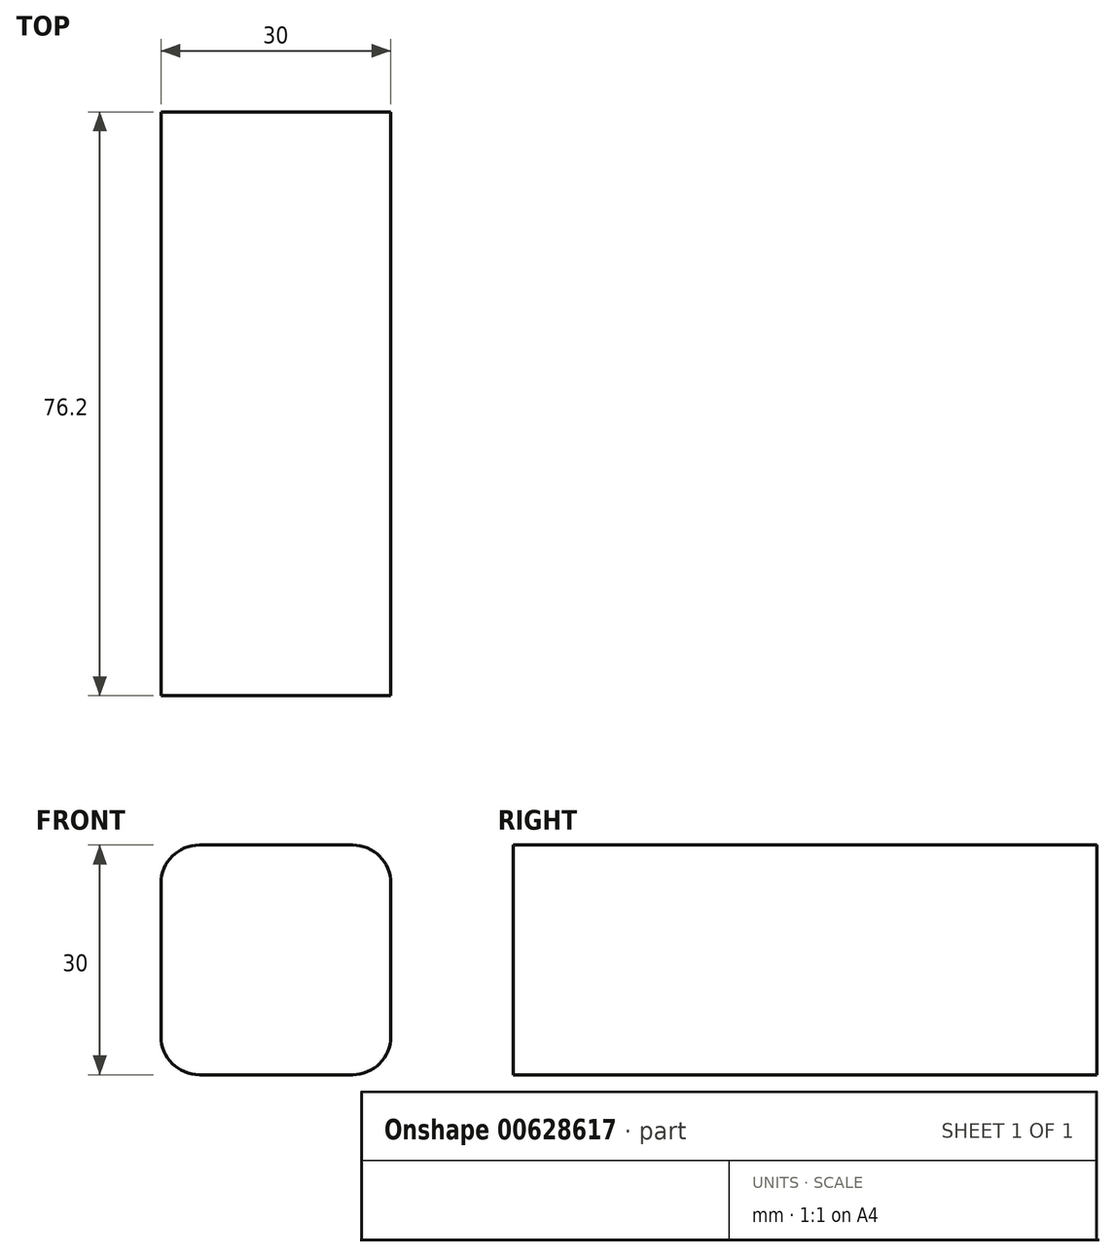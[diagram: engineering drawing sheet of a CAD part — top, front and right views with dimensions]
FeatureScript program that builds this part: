
annotation { "Feature Type Name" : "Feature", "Feature Type Description" : "" }
export const myFeature = defineFeature(function(context is Context, id is Id, definition is map)
    precondition{}
    {
        {
            var Q0;
            Q0=qCreatedBy(makeId("Front.planeOp"),FACE);
            var sketch = newSketch(context, id + "F0", { "sketchPlane" : qUnion([Q0])});
            skLineSegment(sketch, "E0.bottom", {"start": v(-92.2, 23.85) * mm, "end": v(-62.2, 23.85) * mm});
            skLineSegment(sketch, "E0.top", {"start": v(-92.2, -6.15) * mm, "end": v(-62.2, -6.15) * mm});
            skLineSegment(sketch, "E0.left", {"start": v(-92.2, 23.85) * mm, "end": v(-92.2, -6.15) * mm});
            skLineSegment(sketch, "E0.right", {"start": v(-62.2, 23.85) * mm, "end": v(-62.2, -6.15) * mm});
            skSolve(sketch);
        }
        {
            var Q0;
            Q0 = qSketchRegion(id + "F0", true);
            extrude(context, id + "F1", {"entities" : qUnion([Q0]), "depth" : 76.2 * mm, "offsetDistance" : 25.4 * mm});
        }
        {
            var Q0;
            Q0=makeQuery(id+"F1.opExtrude","SWEPT_EDGE",EDGE,{"disambiguationData":[OSD([sQuery(id+"F0.wireOp",EDGE,"E0.bottom"),sQuery(id+"F0.wireOp",EDGE,"E0.right")])]});
            var Q1;
            Q1=makeQuery(id+"F1.opExtrude","SWEPT_EDGE",EDGE,{"disambiguationData":[OSD([sQuery(id+"F0.wireOp",EDGE,"E0.bottom"),sQuery(id+"F0.wireOp",EDGE,"E0.left")])]});
            var Q2;
            Q2=makeQuery(id+"F1.opExtrude","SWEPT_EDGE",EDGE,{"disambiguationData":[OSD([sQuery(id+"F0.wireOp",EDGE,"E0.top"),sQuery(id+"F0.wireOp",EDGE,"E0.right")])]});
            var Q3;
            Q3=makeQuery(id+"F1.opExtrude","SWEPT_EDGE",EDGE,{"disambiguationData":[OSD([sQuery(id+"F0.wireOp",EDGE,"E0.top"),sQuery(id+"F0.wireOp",EDGE,"E0.left")])]});
            fillet(context, id + "F2", {"entities" : qUnion([Q0, Q1, Q2, Q3]), "radius" : 5 * mm, "tangentPropagation" : true, "allowEdgeOverflow" : false});
        }
    });
